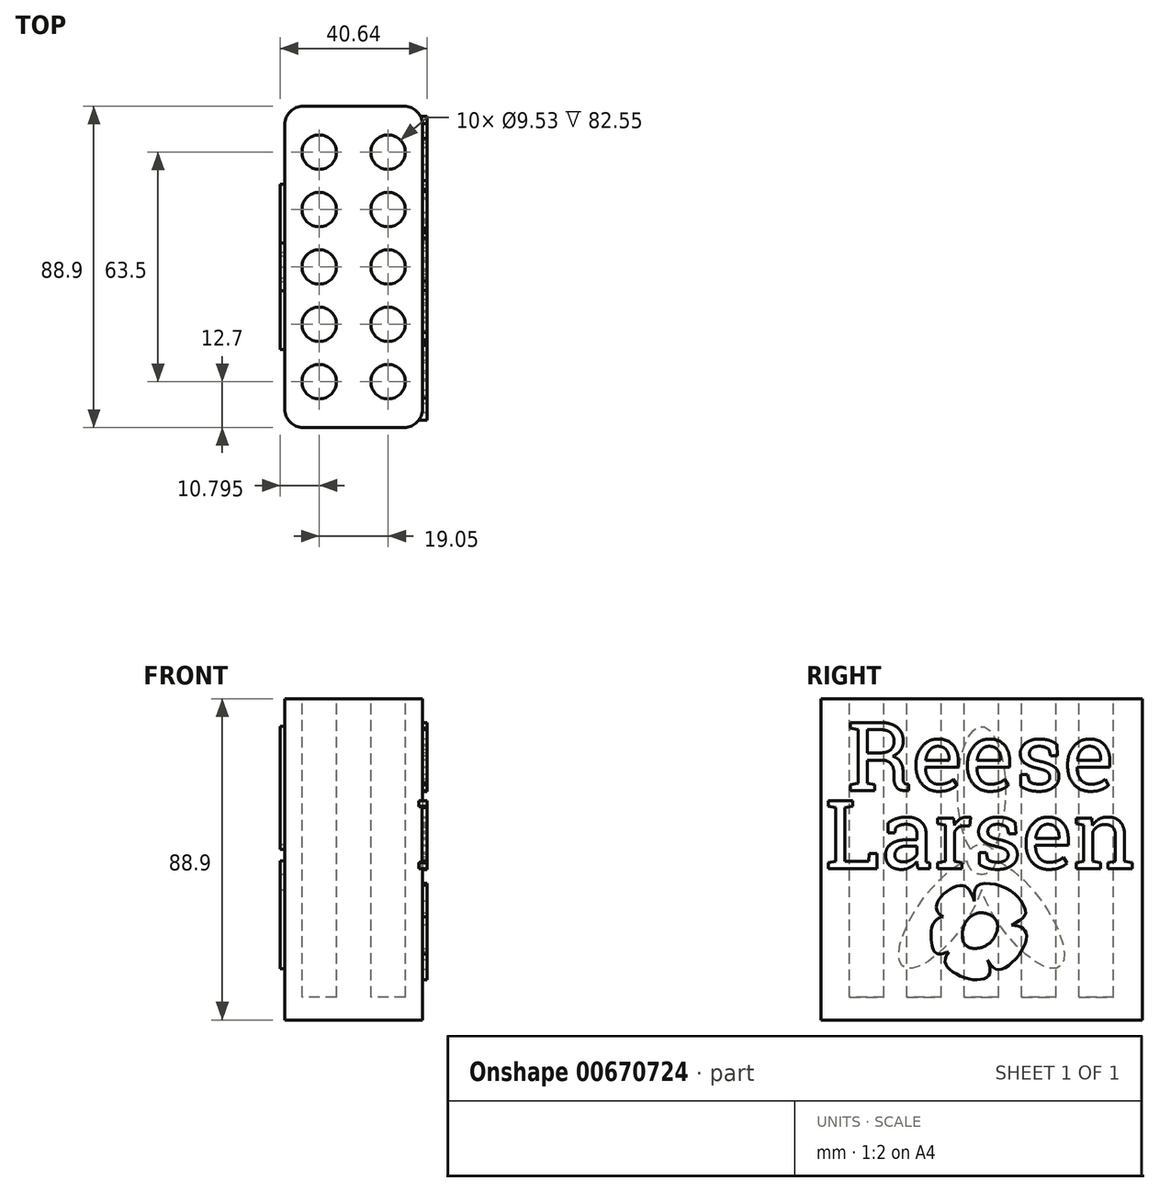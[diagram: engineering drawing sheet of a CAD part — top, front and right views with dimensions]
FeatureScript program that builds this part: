
annotation { "Feature Type Name" : "Feature", "Feature Type Description" : "" }
export const myFeature = defineFeature(function(context is Context, id is Id, definition is map)
    precondition{}
    {
        {
            var Q0;
            Q0=qCreatedBy(makeId("Right.planeOp"),FACE);
            var sketch = newSketch(context, id + "F0", { "sketchPlane" : qUnion([Q0])});
            skLineSegment(sketch, "E0.bottom", {"start": v(-44.45, 44.45) * mm, "end": v(44.45, 44.45) * mm});
            skLineSegment(sketch, "E0.top", {"start": v(-44.45, -44.45) * mm, "end": v(44.45, -44.45) * mm});
            skLineSegment(sketch, "E0.left", {"start": v(-44.45, 44.45) * mm, "end": v(-44.45, -44.45) * mm});
            skLineSegment(sketch, "E0.right", {"start": v(44.45, 44.45) * mm, "end": v(44.45, -44.45) * mm});
            skPoint(sketch, "E0.middle", {"position": v(0, 0) * mm});
            skSolve(sketch);
        }
        {
            var Q0;
            Q0=qSketchRegion(id+"F0",true);
            extrude(context, id + "F1", {"entities" : qUnion([Q0]), "endBound" : BoundingType.SYMMETRIC, "depth" : 38.1 * mm, "offsetDistance" : 25.4 * mm});
        }
        {
            var Q0;
            Q0=makeQuery(id+"F1.opExtrude","SWEPT_FACE",FACE,{"disambiguationData":[OSD([sQuery(id+"F0.wireOp",EDGE,"E0.bottom")])]});
            var sketch = newSketch(context, id + "F2", { "sketchPlane" : qUnion([Q0])});
            skCircle(sketch, "E1", {"center": v(-9.52, -31.75) * mm, "radius": 4.76 * mm});
            skCircle(sketch, "E2", {"center": v(-9.52, 0) * mm, "radius": 4.76 * mm});
            skCircle(sketch, "E3", {"center": v(-9.52, -15.88) * mm, "radius": 4.76 * mm});
            skCircle(sketch, "E4", {"center": v(-9.52, 15.88) * mm, "radius": 4.76 * mm});
            skCircle(sketch, "E5", {"center": v(-9.52, 31.75) * mm, "radius": 4.76 * mm});
            skCircle(sketch, "E6.MirrorC", {"center": v(9.52, 0) * mm, "radius": 4.76 * mm});
            skCircle(sketch, "E7.MirrorC", {"center": v(9.52, -31.75) * mm, "radius": 4.76 * mm});
            skCircle(sketch, "E8.MirrorC", {"center": v(9.52, -15.88) * mm, "radius": 4.76 * mm});
            skCircle(sketch, "E9.MirrorC", {"center": v(9.52, 15.88) * mm, "radius": 4.76 * mm});
            skCircle(sketch, "E10.MirrorC", {"center": v(9.52, 31.75) * mm, "radius": 4.76 * mm});
            skSolve(sketch);
        }
        {
            var Q0;
            Q0=qSketchRegion(id+"F2",true);
            extrude(context, id + "F3", {"entities" : qUnion([Q0]), "operationType" : NewBodyOperationType.REMOVE, "oppositeDirection" : true, "depth" : 82.55 * mm, "offsetDistance" : 25.4 * mm});
        }
        {
            var Q0;
            Q0=makeQuery(id+"F1.opExtrude","CAP_FACE",FACE,{"disambiguationData":[OSD([sQuery(id+"F0.wireOp",EDGE,"E0.bottom"),sQuery(id+"F0.wireOp",EDGE,"E0.top"),sQuery(id+"F0.wireOp",EDGE,"E0.left"),sQuery(id+"F0.wireOp",EDGE,"E0.right")])],"isStart":false});
            var sketch = newSketch(context, id + "F4", { "sketchPlane" : qUnion([Q0])});
            skText(sketch, "E11", { "text": "Reese", "fontName": "RobotoSlab-Regular.ttf"});
            skText(sketch, "E12", { "text": "Larsen", "fontName": "RobotoSlab-Regular.ttf"});
            const initialGuessF4  = {"E11": [-0.03718, 0.01905, 1, 0, 0.01905], "E12": [-0.04335, -0.00254, 1, 0, 0.01905]};
            skSetInitialGuess(sketch, initialGuessF4);
            skSolve(sketch);
        }
        {
            var Q0;
            Q0=qSketchRegion(id+"F4",true);
            extrude(context, id + "F5", {"entities" : qUnion([Q0]), "operationType" : NewBodyOperationType.ADD, "depth" : 1.27 * mm, "offsetDistance" : 25.4 * mm});
        }
        {
            var Q0;
            Q0=makeQuery(id+"F1.opExtrude","CAP_EDGE",EDGE,{"disambiguationData":[OSD([sQuery(id+"F0.wireOp",EDGE,"E0.left")])],"isStart":false});
            var Q1;
            Q1=makeQuery(id+"F1.opExtrude","CAP_EDGE",EDGE,{"disambiguationData":[OSD([sQuery(id+"F0.wireOp",EDGE,"E0.right")])],"isStart":false});
            var Q2;
            Q2=makeQuery(id+"F1.opExtrude","CAP_EDGE",EDGE,{"disambiguationData":[OSD([sQuery(id+"F0.wireOp",EDGE,"E0.right")])],"isStart":true});
            var Q3;
            Q3=makeQuery(id+"F1.opExtrude","CAP_EDGE",EDGE,{"disambiguationData":[OSD([sQuery(id+"F0.wireOp",EDGE,"E0.left")])],"isStart":true});
            fillet(context, id + "F6", {"entities" : qUnion([Q0, Q1, Q2, Q3]), "radius" : 5.08 * mm, "tangentPropagation" : true, "allowEdgeOverflow" : false});
        }
        {
            var Q0;
            {var subQ0=sQuery(id+"F0.wireOp",EDGE,"E0.right");var subQ1=sQuery(id+"F0.wireOp",EDGE,"E0.left");var subQ2=sQuery(id+"F0.wireOp",EDGE,"E0.top");var subQ3=sQuery(id+"F0.wireOp",EDGE,"E0.bottom");Q0=makeQuery(id+"F5.boolean.opBoolean","SPLIT",FACE,{"disambiguationData":[TD([makeQuery(id+"F1.opExtrude","SWEPT_FACE",FACE,{"disambiguationData":[OSD([subQ3])]})])],"derivedFrom":makeQuery(id+"F1.opExtrude","CAP_FACE",FACE,{"disambiguationData":[OSD([subQ3,subQ2,subQ1,subQ0])],"isStart":false})});}
            var sketch = newSketch(context, id + "F7", { "sketchPlane" : qUnion([Q0])});
            skFitSpline(sketch, "E13", {"points": [v(-4.86, -18.4) * mm, v(-4.86, -23.15) * mm, v(-2.54, -24.6) * mm, v(1.63, -23.63) * mm, v(4.35, -19.56) * mm, v(3.48, -16.16) * mm, v(-1.08, -14.9) * mm, v(-4.86, -18.4) * mm]});
            skFitSpline(sketch, "E14", {"points": [v(-1.08, -14.9) * mm, v(-2.63, -9.86) * mm, v(-5.16, -7.24) * mm, v(-10.68, -9.86) * mm, v(-12.53, -13.64) * mm, v(-10.68, -15.97) * mm], "startDerivative": vector(-5.93, 23.88) * mm, "endDerivative": vector(15.22, -12.78) * mm});
            skFitSpline(sketch, "E15", {"points": [v(-4.47, -17.57) * mm, v(-10.68, -15.97) * mm, v(-13.6, -18.4) * mm, v(-13.5, -24.5) * mm, v(-11.85, -26.25) * mm, v(-4.86, -23.15) * mm], "startDerivative": vector(-29.8, 12.2) * mm, "endDerivative": vector(33.44, 19.83) * mm});
            skFitSpline(sketch, "E16", {"points": [v(-9.16, -25.52) * mm, v(-9.89, -29.04) * mm, v(-2.87, -33.2) * mm, v(2.18, -31.73) * mm, v(0, -24.4) * mm], "startDerivative": vector(-9.58, -18.07) * mm, "endDerivative": vector(-15.48, 30.39) * mm});
            skFitSpline(sketch, "E17", {"points": [v(1.63, -27.8) * mm, v(4.55, -30.51) * mm, v(10.58, -26.1) * mm, v(12.21, -20.07) * mm, v(9.2, -18.28) * mm, v(4.44, -18.85) * mm], "startDerivative": vector(13.9, -22.16) * mm, "endDerivative": vector(-25, -5.78) * mm});
            skFitSpline(sketch, "E18", {"points": [v(-2, -11.56) * mm, v(-1, -7.27) * mm, v(6.67, -7.92) * mm, v(11.4, -12.32) * mm, v(12.05, -15.34) * mm, v(8.3, -18.23) * mm], "startDerivative": vector(-1.04, 28.17) * mm, "endDerivative": vector(-25.73, -13.95) * mm});
            skSolve(sketch);
        }
        {
            var Q0;
            Q0 = qSketchRegion(id + "F7", true);
            extrude(context, id + "F8", {"entities" : qUnion([Q0]), "operationType" : NewBodyOperationType.ADD, "depth" : 1.27 * mm, "offsetDistance" : 25.4 * mm});
        }
        {
            var Q0;
            Q0=makeQuery(id+"F1.opExtrude","CAP_FACE",FACE,{"disambiguationData":[OSD([sQuery(id+"F0.wireOp",EDGE,"E0.bottom"),sQuery(id+"F0.wireOp",EDGE,"E0.top"),sQuery(id+"F0.wireOp",EDGE,"E0.left"),sQuery(id+"F0.wireOp",EDGE,"E0.right")])],"isStart":true});
            var sketch = newSketch(context, id + "F9", { "sketchPlane" : qUnion([Q0])});
            skCircle(sketch, "E19", {"center": v(0, 0) * mm, "radius": 4.09 * mm});
            skEllipse(sketch, "E20", {"center": v(0, 18.77) * mm, "majorRadius": 18 * mm, "minorRadius": 6.64 * mm, "majorAxis": v(0, 1)});
            skEllipse(sketch, "E21.1.0", {"center": v(-17.85, 5.8) * mm, "majorRadius": 18 * mm, "minorRadius": 6.64 * mm, "majorAxis": v(-0.95, 0.3)});
            skEllipse(sketch, "E21.2.0", {"center": v(-11.03, -15.19) * mm, "majorRadius": 18 * mm, "minorRadius": 6.64 * mm, "majorAxis": v(-0.59, -0.8)});
            skEllipse(sketch, "E21.3.0", {"center": v(11.03, -15.19) * mm, "majorRadius": 18 * mm, "minorRadius": 6.64 * mm, "majorAxis": v(0.59, -0.8)});
            skEllipse(sketch, "E21.4.0", {"center": v(17.85, 5.8) * mm, "majorRadius": 18 * mm, "minorRadius": 6.64 * mm, "majorAxis": v(0.95, 0.3)});
            skSolve(sketch);
        }
        {
            var Q0;
            {var subQ0=sQuery(id+"F9.wireOp",EDGE,"E21.4.0");var subQ1=sQuery(id+"F9.wireOp",EDGE,"E19");var subQ2=makeQuery(id+"F9.imprint","INTERSECT",VERTEX,{"disambiguationData":[OD(0.0)],"derivedFrom":[subQ1,subQ0]});Q0=makeQuery(id+"F9.imprint","IMPRINT",FACE,{"disambiguationData":[TD([[makeQuery(id+"F9.imprint","IMPRINT",EDGE,{"disambiguationData":[TD([[subQ2,-1.0]])],"derivedFrom":subQ1}),-1.0]])]});}
            var Q1;
            {var subQ0=sQuery(id+"F9.wireOp",EDGE,"E20");var subQ1=sQuery(id+"F9.wireOp",EDGE,"E19");var subQ2=makeQuery(id+"F9.imprint","INTERSECT",VERTEX,{"disambiguationData":[OD(1.0)],"derivedFrom":[subQ1,subQ0]});Q1=makeQuery(id+"F9.imprint","IMPRINT",FACE,{"disambiguationData":[TD([[makeQuery(id+"F9.imprint","IMPRINT",EDGE,{"disambiguationData":[TD([[subQ2,-1.0]])],"derivedFrom":subQ1}),-1.0]])]});}
            var Q2;
            {var subQ0=sQuery(id+"F9.wireOp",EDGE,"E21.1.0");var subQ1=sQuery(id+"F9.wireOp",EDGE,"E19");var subQ2=makeQuery(id+"F9.imprint","INTERSECT",VERTEX,{"disambiguationData":[OD(1.0)],"derivedFrom":[subQ1,subQ0]});Q2=makeQuery(id+"F9.imprint","IMPRINT",FACE,{"disambiguationData":[TD([[makeQuery(id+"F9.imprint","IMPRINT",EDGE,{"disambiguationData":[TD([[subQ2,-1.0]])],"derivedFrom":subQ1}),-1.0]])]});}
            var Q3;
            {var subQ0=sQuery(id+"F9.wireOp",EDGE,"E21.2.0");var subQ1=sQuery(id+"F9.wireOp",EDGE,"E19");var subQ2=makeQuery(id+"F9.imprint","INTERSECT",VERTEX,{"disambiguationData":[OD(1.0)],"derivedFrom":[subQ1,subQ0]});Q3=makeQuery(id+"F9.imprint","IMPRINT",FACE,{"disambiguationData":[TD([[makeQuery(id+"F9.imprint","IMPRINT",EDGE,{"disambiguationData":[TD([[subQ2,-1.0]])],"derivedFrom":subQ1}),-1.0]])]});}
            var Q4;
            {var subQ0=sQuery(id+"F9.wireOp",EDGE,"E20");var subQ1=sQuery(id+"F9.wireOp",EDGE,"E19");var subQ2=makeQuery(id+"F9.imprint","INTERSECT",VERTEX,{"disambiguationData":[OD(0.0)],"derivedFrom":[subQ1,subQ0]});Q4=makeQuery(id+"F9.imprint","IMPRINT",FACE,{"disambiguationData":[TD([[makeQuery(id+"F9.imprint","IMPRINT",EDGE,{"disambiguationData":[TD([[subQ2,1.0]])],"derivedFrom":subQ1}),-1.0]])]});}
            var Q5;
            {var subQ0=sQuery(id+"F9.wireOp",EDGE,"E21.1.0");var subQ1=sQuery(id+"F9.wireOp",EDGE,"E19");var subQ2=makeQuery(id+"F9.imprint","INTERSECT",VERTEX,{"disambiguationData":[OD(0.0)],"derivedFrom":[subQ1,subQ0]});Q5=makeQuery(id+"F9.imprint","IMPRINT",FACE,{"disambiguationData":[TD([[makeQuery(id+"F9.imprint","IMPRINT",EDGE,{"disambiguationData":[TD([[subQ2,-1.0]])],"derivedFrom":subQ1}),-1.0]])]});}
            var Q6;
            {var subQ0=sQuery(id+"F9.wireOp",EDGE,"E21.2.0");var subQ1=sQuery(id+"F9.wireOp",EDGE,"E19");var subQ2=makeQuery(id+"F9.imprint","INTERSECT",VERTEX,{"disambiguationData":[OD(0.0)],"derivedFrom":[subQ1,subQ0]});Q6=makeQuery(id+"F9.imprint","IMPRINT",FACE,{"disambiguationData":[TD([[makeQuery(id+"F9.imprint","IMPRINT",EDGE,{"disambiguationData":[TD([[subQ2,-1.0]])],"derivedFrom":subQ1}),-1.0]])]});}
            var Q7;
            {var subQ0=sQuery(id+"F9.wireOp",EDGE,"E21.3.0");var subQ1=sQuery(id+"F9.wireOp",EDGE,"E19");var subQ2=makeQuery(id+"F9.imprint","INTERSECT",VERTEX,{"disambiguationData":[OD(0.0)],"derivedFrom":[subQ1,subQ0]});Q7=makeQuery(id+"F9.imprint","IMPRINT",FACE,{"disambiguationData":[TD([[makeQuery(id+"F9.imprint","IMPRINT",EDGE,{"disambiguationData":[TD([[subQ2,-1.0]])],"derivedFrom":subQ1}),-1.0]])]});}
            var Q8;
            {var subQ0=sQuery(id+"F9.wireOp",EDGE,"E21.4.0");var subQ1=sQuery(id+"F9.wireOp",EDGE,"E19");var subQ2=makeQuery(id+"F9.imprint","INTERSECT",VERTEX,{"disambiguationData":[OD(1.0)],"derivedFrom":[subQ1,subQ0]});Q8=makeQuery(id+"F9.imprint","IMPRINT",FACE,{"disambiguationData":[TD([[makeQuery(id+"F9.imprint","IMPRINT",EDGE,{"disambiguationData":[TD([[subQ2,-1.0]])],"derivedFrom":subQ1}),-1.0]])]});}
            var Q9;
            {var subQ0=sQuery(id+"F9.wireOp",EDGE,"E21.4.0");var subQ1=sQuery(id+"F9.wireOp",EDGE,"E19");var subQ2=makeQuery(id+"F9.imprint","INTERSECT",VERTEX,{"disambiguationData":[OD(0.0)],"derivedFrom":[subQ1,subQ0]});Q9=makeQuery(id+"F9.imprint","IMPRINT",FACE,{"disambiguationData":[TD([[makeQuery(id+"F9.imprint","IMPRINT",EDGE,{"disambiguationData":[TD([[subQ2,1.0]])],"derivedFrom":subQ1}),-1.0]])]});}
            extrude(context, id + "F10", {"entities" : qUnion([Q0, Q1, Q2, Q3, Q4, Q5, Q6, Q7, Q8, Q9]), "operationType" : NewBodyOperationType.ADD, "depth" : 1.27 * mm, "offsetDistance" : 25.4 * mm});
        }
    });
